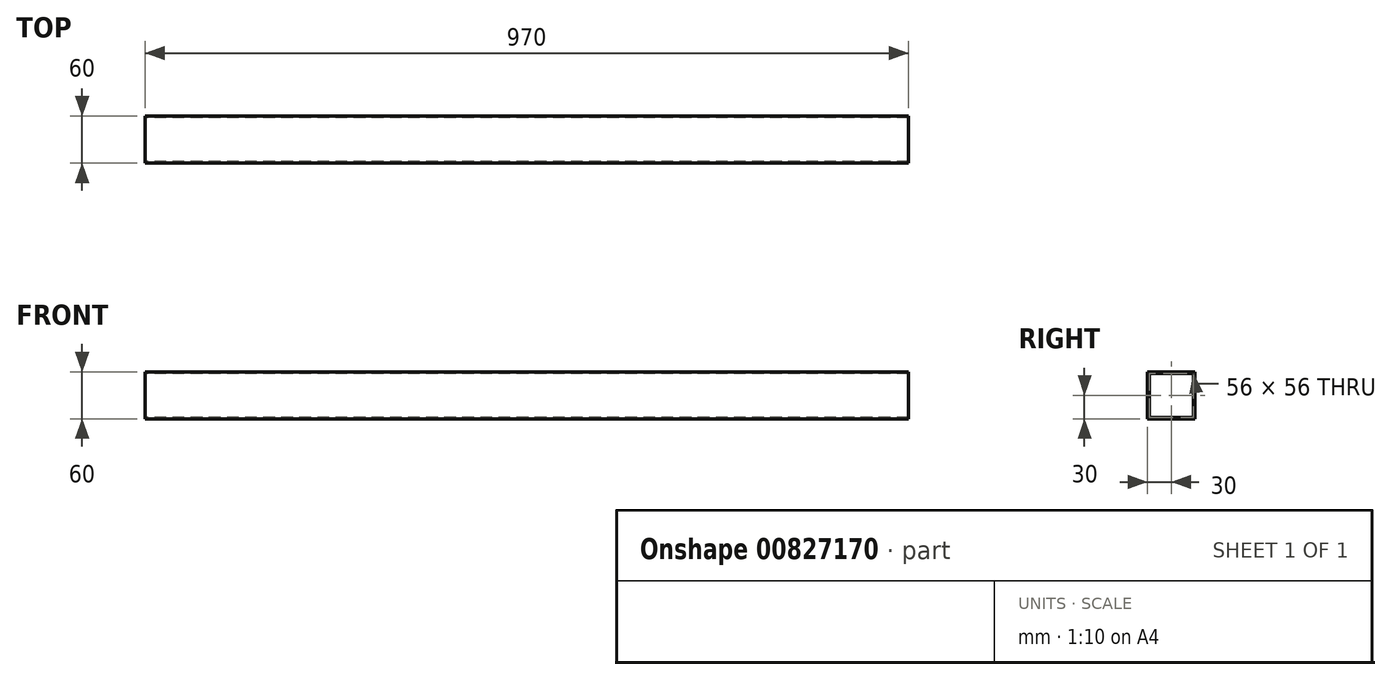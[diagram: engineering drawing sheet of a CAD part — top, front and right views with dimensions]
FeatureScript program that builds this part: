
annotation { "Feature Type Name" : "Feature", "Feature Type Description" : "" }
export const myFeature = defineFeature(function(context is Context, id is Id, definition is map)
    precondition{}
    {
        {
            var Q0;
            Q0=qCreatedBy(makeId("Right.planeOp"),FACE);
            var sketch = newSketch(context, id + "F0", { "sketchPlane" : qUnion([Q0])});
            skLineSegment(sketch, "E0.bottom", {"start": v(30, 30) * mm, "end": v(-30, 30) * mm});
            skLineSegment(sketch, "E0.top", {"start": v(30, -30) * mm, "end": v(-30, -30) * mm});
            skLineSegment(sketch, "E0.left", {"start": v(30, 30) * mm, "end": v(30, -30) * mm});
            skLineSegment(sketch, "E0.right", {"start": v(-30, 30) * mm, "end": v(-30, -30) * mm});
            skPoint(sketch, "E0.middle", {"position": v(0, 0) * mm});
            skLineSegment(sketch, "E1.bottom", {"start": v(28, 28) * mm, "end": v(-28, 28) * mm});
            skLineSegment(sketch, "E1.top", {"start": v(28, -28) * mm, "end": v(-28, -28) * mm});
            skLineSegment(sketch, "E1.left", {"start": v(28, 28) * mm, "end": v(28, -28) * mm});
            skLineSegment(sketch, "E1.right", {"start": v(-28, 28) * mm, "end": v(-28, -28) * mm});
            skSolve(sketch);
        }
        {
            var Q0;
            Q0=makeQuery(id+"F0.imprint","IMPRINT",FACE,{"disambiguationData":[TD([[makeQuery(id+"F0.imprint","IMPRINT",EDGE,{"derivedFrom":sQuery(id+"F0.wireOp",EDGE,"E0.bottom")}),1.0]])]});
            extrude(context, id + "F1", {"entities" : qUnion([Q0]), "depth" : 970 * mm, "offsetDistance" : 25 * mm});
        }
    });
